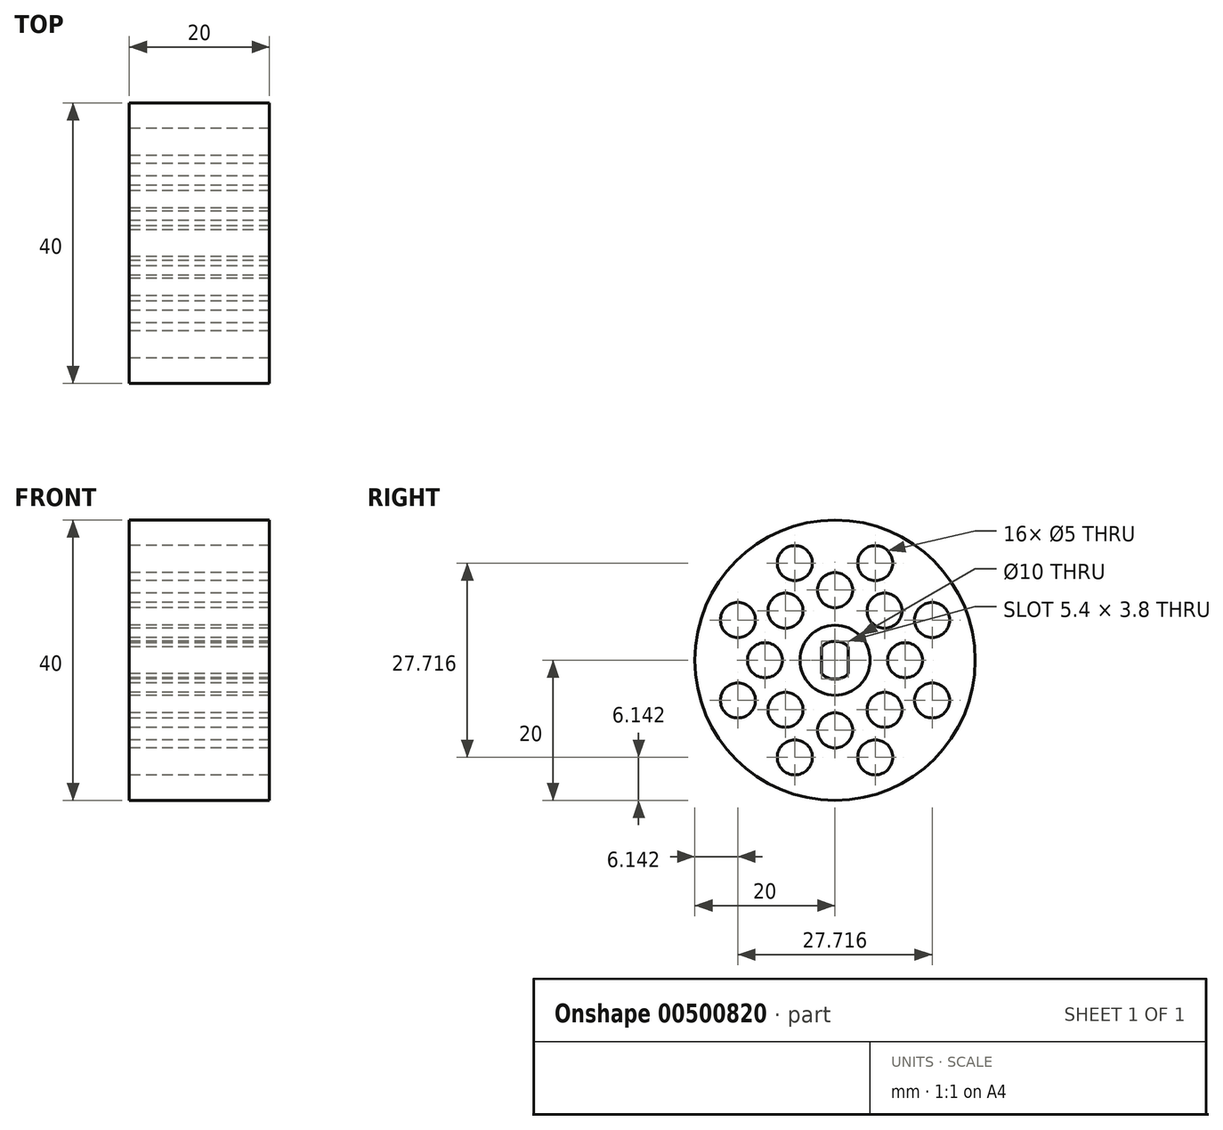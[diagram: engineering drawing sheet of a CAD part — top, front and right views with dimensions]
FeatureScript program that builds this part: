
annotation { "Feature Type Name" : "Feature", "Feature Type Description" : "" }
export const myFeature = defineFeature(function(context is Context, id is Id, definition is map)
    precondition{}
    {
        {
            var Q0;
            Q0=qCreatedBy(makeId("Right.planeOp"),FACE);
            var sketch = newSketch(context, id + "F0", { "sketchPlane" : qUnion([Q0])});
            skCircle(sketch, "E0", {"center": v(0, 0) * mm, "radius": 5 * mm});
            skArc(sketch, "E1", {"start": v(-1.9, -1.92) * mm, "mid": v(0, -2.7) * mm, "end": v(1.9, -1.92) * mm});
            skLineSegment(sketch, "E2.left", {"start": v(1.9, 1.92) * mm, "end": v(1.9, -1.92) * mm});
            skLineSegment(sketch, "E2.right", {"start": v(-1.9, 1.92) * mm, "end": v(-1.9, -1.92) * mm});
            skArc(sketch, "E3.trimOffspring", {"start": v(1.9, 1.92) * mm, "mid": v(0, 2.7) * mm, "end": v(-1.9, 1.92) * mm});
            skCircle(sketch, "E4.0", {"center": v(0, 0) * mm, "radius": 20 * mm});
            skCircle(sketch, "E5", {"center": v(0, 0) * mm, "radius": 10 * mm, "construction": true});
            skCircle(sketch, "E6", {"center": v(10, 0) * mm, "radius": 2.5 * mm});
            skCircle(sketch, "E7.1.0", {"center": v(7.07, 7.07) * mm, "radius": 2.5 * mm});
            skCircle(sketch, "E7.2.0", {"center": v(0, 10) * mm, "radius": 2.5 * mm});
            skCircle(sketch, "E7.3.0", {"center": v(-7.07, 7.07) * mm, "radius": 2.5 * mm});
            skCircle(sketch, "E7.4.0", {"center": v(-10, 0) * mm, "radius": 2.5 * mm});
            skCircle(sketch, "E7.5.0", {"center": v(-7.07, -7.07) * mm, "radius": 2.5 * mm});
            skCircle(sketch, "E7.6.0", {"center": v(0, -10) * mm, "radius": 2.5 * mm});
            skCircle(sketch, "E7.7.0", {"center": v(7.07, -7.07) * mm, "radius": 2.5 * mm});
            skCircle(sketch, "E8", {"center": v(0, 0) * mm, "radius": 15 * mm, "construction": true});
            skCircle(sketch, "E9", {"center": v(5.74, 13.86) * mm, "radius": 2.5 * mm});
            skLineSegment(sketch, "E10", {"start": v(0, 0) * mm, "end": v(5.74, 13.86) * mm, "construction": true});
            skCircle(sketch, "E11.1.0", {"center": v(-5.74, 13.86) * mm, "radius": 2.5 * mm});
            skCircle(sketch, "E11.2.0", {"center": v(-13.86, 5.74) * mm, "radius": 2.5 * mm});
            skCircle(sketch, "E11.3.0", {"center": v(-13.86, -5.74) * mm, "radius": 2.5 * mm});
            skCircle(sketch, "E11.4.0", {"center": v(-5.74, -13.86) * mm, "radius": 2.5 * mm});
            skCircle(sketch, "E11.5.0", {"center": v(5.74, -13.86) * mm, "radius": 2.5 * mm});
            skCircle(sketch, "E11.6.0", {"center": v(13.86, -5.74) * mm, "radius": 2.5 * mm});
            skCircle(sketch, "E11.7.0", {"center": v(13.86, 5.74) * mm, "radius": 2.5 * mm});
            skSolve(sketch);
        }
        {
            var Q0;
            Q0=makeQuery(id+"F0.imprint","IMPRINT",FACE,{"disambiguationData":[TD([[makeQuery(id+"F0.imprint","IMPRINT",EDGE,{"derivedFrom":sQuery(id+"F0.wireOp",EDGE,"E0")}),1.0]])]});
            extrude(context, id + "F1", {"entities" : qUnion([Q0]), "offsetDistance" : 25 * mm, "depth" : 20 * mm});
        }
        {
            var Q0;
            Q0 = qSketchRegion(id + "F0", true);
            var Q1;
            Q1=makeQuery(id+"F1.opExtrude","CAP_FACE",FACE,{"disambiguationData":[OSD([sQuery(id+"F0.wireOp",EDGE,"E0"),sQuery(id+"F0.wireOp",EDGE,"E1"),sQuery(id+"F0.wireOp",EDGE,"E2.left"),sQuery(id+"F0.wireOp",EDGE,"E2.right"),sQuery(id+"F0.wireOp",EDGE,"E3.trimOffspring")])],"isStart":false});
            extrude(context, id + "F2", {"entities" : qUnion([Q0]), "endBound" : BoundingType.UP_TO_SURFACE, "endBoundEntityFace" : qUnion([Q1]), "offsetDistance" : 25 * mm, "depth" : 25 * mm});
        }
    });
